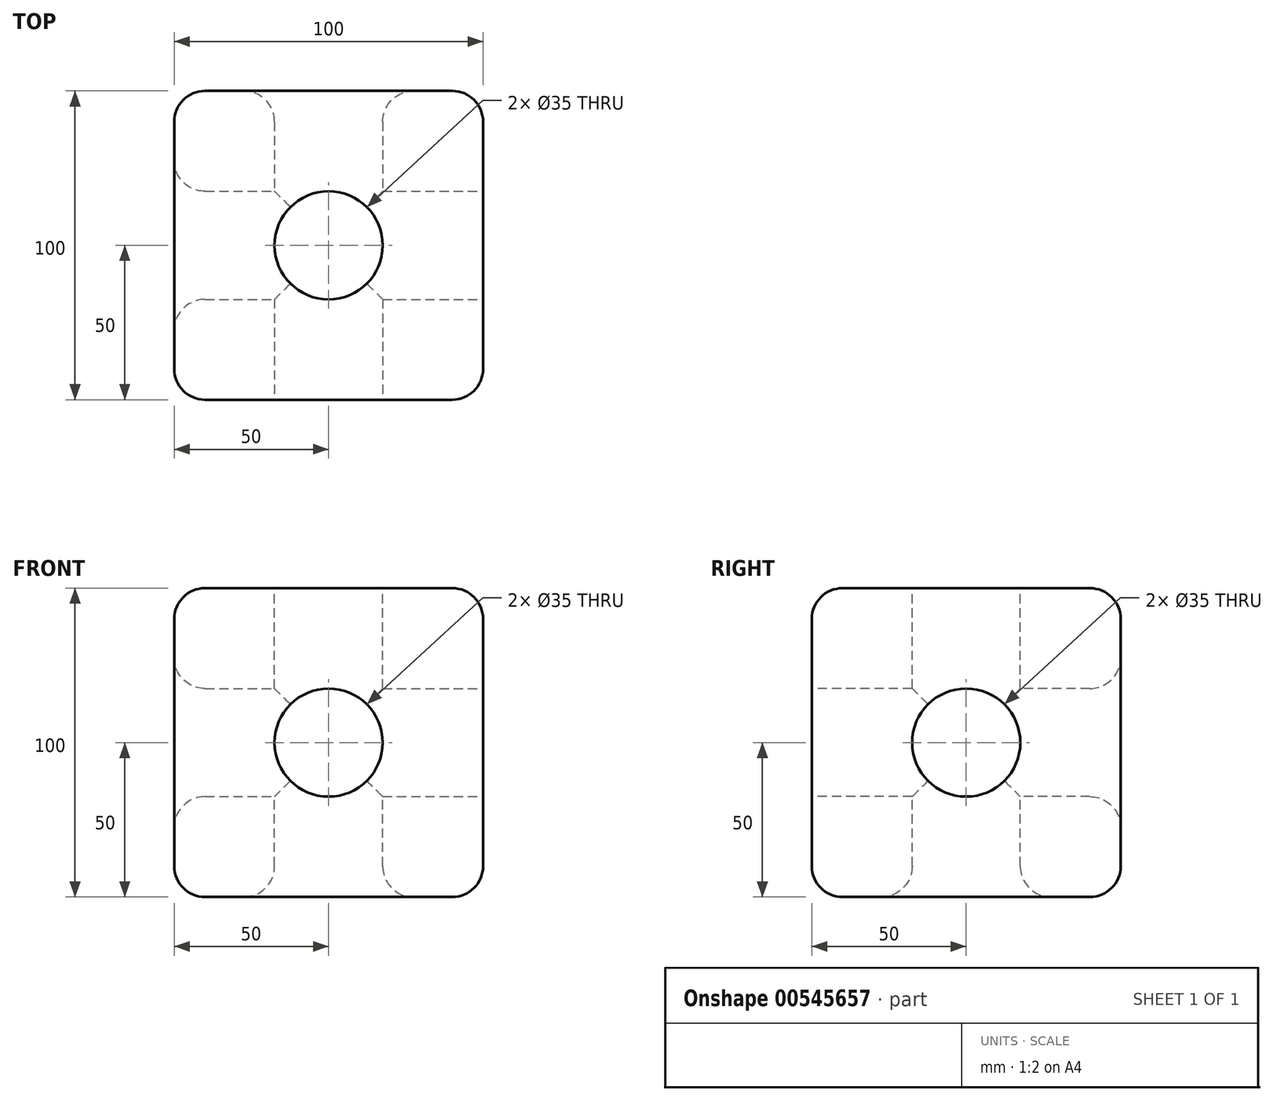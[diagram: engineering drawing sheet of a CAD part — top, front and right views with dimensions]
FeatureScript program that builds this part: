
annotation { "Feature Type Name" : "Feature", "Feature Type Description" : "" }
export const myFeature = defineFeature(function(context is Context, id is Id, definition is map)
    precondition{}
    {
        {
            var Q0;
            Q0=qCreatedBy(makeId("Front.planeOp"),FACE);
            var sketch = newSketch(context, id + "F0", { "sketchPlane" : qUnion([Q0])});
            skLineSegment(sketch, "E0.bottom", {"start": v(50, 50) * mm, "end": v(-50, 50) * mm});
            skLineSegment(sketch, "E0.top", {"start": v(50, -50) * mm, "end": v(-50, -50) * mm});
            skLineSegment(sketch, "E0.left", {"start": v(50, 50) * mm, "end": v(50, -50) * mm});
            skLineSegment(sketch, "E0.right", {"start": v(-50, 50) * mm, "end": v(-50, -50) * mm});
            skPoint(sketch, "E0.middle", {"position": v(0, 0) * mm});
            skSolve(sketch);
        }
        {
            var Q0;
            Q0=makeQuery(id+"F0.imprint","IMPRINT",FACE,{"disambiguationData":[TD([[makeQuery(id+"F0.imprint","IMPRINT",EDGE,{"derivedFrom":sQuery(id+"F0.wireOp",EDGE,"E0.bottom")}),1.0]])]});
            extrude(context, id + "F1", {"entities" : qUnion([Q0]), "endBound" : BoundingType.SYMMETRIC, "depth" : 100 * mm, "offsetDistance" : 25 * mm});
        }
        {
            var Q0;
            Q0=makeQuery(id+"F1.opExtrude","CAP_FACE",FACE,{"disambiguationData":[OSD([sQuery(id+"F0.wireOp",EDGE,"E0.bottom"),sQuery(id+"F0.wireOp",EDGE,"E0.top"),sQuery(id+"F0.wireOp",EDGE,"E0.left"),sQuery(id+"F0.wireOp",EDGE,"E0.right")])],"isStart":false});
            var sketch = newSketch(context, id + "F2", { "sketchPlane" : qUnion([Q0])});
            skCircle(sketch, "E1", {"center": v(0, 0) * mm, "radius": 17.5 * mm});
            skSolve(sketch);
        }
        {
            var Q0;
            Q0=makeQuery(id+"F2.imprint","IMPRINT",FACE,{"disambiguationData":[TD([[makeQuery(id+"F2.imprint","IMPRINT",EDGE,{"derivedFrom":sQuery(id+"F2.wireOp",EDGE,"E1")}),1.0]])]});
            extrude(context, id + "F3", {"entities" : qUnion([Q0]), "operationType" : NewBodyOperationType.REMOVE, "endBound" : BoundingType.THROUGH_ALL, "oppositeDirection" : true, "depth" : 25 * mm, "offsetDistance" : 25 * mm});
        }
        {
            var Q0;
            Q0=makeQuery(id+"F1.opExtrude","SWEPT_FACE",FACE,{"disambiguationData":[OSD([sQuery(id+"F0.wireOp",EDGE,"E0.left")])]});
            var sketch = newSketch(context, id + "F4", { "sketchPlane" : qUnion([Q0])});
            skCircle(sketch, "E2", {"center": v(0, 0) * mm, "radius": 17.5 * mm});
            skSolve(sketch);
        }
        {
            var Q0;
            Q0=makeQuery(id+"F4.imprint","IMPRINT",FACE,{"disambiguationData":[TD([[makeQuery(id+"F4.imprint","IMPRINT",EDGE,{"derivedFrom":sQuery(id+"F4.wireOp",EDGE,"E2")}),1.0]])]});
            extrude(context, id + "F5", {"entities" : qUnion([Q0]), "operationType" : NewBodyOperationType.REMOVE, "endBound" : BoundingType.THROUGH_ALL, "oppositeDirection" : true, "depth" : 25 * mm, "offsetDistance" : 25 * mm});
        }
        {
            var Q0;
            Q0=makeQuery(id+"F1.opExtrude","CAP_EDGE",EDGE,{"disambiguationData":[OSD([sQuery(id+"F0.wireOp",EDGE,"E0.bottom")])],"isStart":false});
            var Q1;
            Q1=makeQuery(id+"F1.opExtrude","CAP_EDGE",EDGE,{"disambiguationData":[OSD([sQuery(id+"F0.wireOp",EDGE,"E0.left")])],"isStart":false});
            var Q2;
            Q2=makeQuery(id+"F1.opExtrude","CAP_EDGE",EDGE,{"disambiguationData":[OSD([sQuery(id+"F0.wireOp",EDGE,"E0.top")])],"isStart":false});
            var Q3;
            Q3=makeQuery(id+"F1.opExtrude","CAP_EDGE",EDGE,{"disambiguationData":[OSD([sQuery(id+"F0.wireOp",EDGE,"E0.right")])],"isStart":false});
            var Q4;
            Q4=makeQuery(id+"F1.opExtrude","SWEPT_EDGE",EDGE,{"disambiguationData":[OSD([sQuery(id+"F0.wireOp",EDGE,"E0.top"),sQuery(id+"F0.wireOp",EDGE,"E0.left")])]});
            var Q5;
            Q5=makeQuery(id+"F1.opExtrude","SWEPT_EDGE",EDGE,{"disambiguationData":[OSD([sQuery(id+"F0.wireOp",EDGE,"E0.top"),sQuery(id+"F0.wireOp",EDGE,"E0.right")])]});
            var Q6;
            Q6=makeQuery(id+"F1.opExtrude","CAP_EDGE",EDGE,{"disambiguationData":[OSD([sQuery(id+"F0.wireOp",EDGE,"E0.top")])],"isStart":true});
            var Q7;
            Q7=makeQuery(id+"F1.opExtrude","CAP_EDGE",EDGE,{"disambiguationData":[OSD([sQuery(id+"F0.wireOp",EDGE,"E0.left")])],"isStart":true});
            var Q8;
            Q8=makeQuery(id+"F1.opExtrude","SWEPT_EDGE",EDGE,{"disambiguationData":[OSD([sQuery(id+"F0.wireOp",EDGE,"E0.bottom"),sQuery(id+"F0.wireOp",EDGE,"E0.left")])]});
            var Q9;
            Q9=makeQuery(id+"F1.opExtrude","CAP_EDGE",EDGE,{"disambiguationData":[OSD([sQuery(id+"F0.wireOp",EDGE,"E0.bottom")])],"isStart":true});
            var Q10;
            Q10=makeQuery(id+"F1.opExtrude","CAP_EDGE",EDGE,{"disambiguationData":[OSD([sQuery(id+"F0.wireOp",EDGE,"E0.right")])],"isStart":true});
            var Q11;
            Q11=makeQuery(id+"F1.opExtrude","SWEPT_EDGE",EDGE,{"disambiguationData":[OSD([sQuery(id+"F0.wireOp",EDGE,"E0.bottom"),sQuery(id+"F0.wireOp",EDGE,"E0.right")])]});
            var Q12;
            Q12=makeQuery(id+"F3.boolean.opBoolean","INTERSECT",EDGE,{"derivedFrom":[makeQuery(id+"F1.opExtrude","CAP_FACE",FACE,{"disambiguationData":[OSD([sQuery(id+"F0.wireOp",EDGE,"E0.bottom"),sQuery(id+"F0.wireOp",EDGE,"E0.top"),sQuery(id+"F0.wireOp",EDGE,"E0.left"),sQuery(id+"F0.wireOp",EDGE,"E0.right")])],"isStart":true}),makeQuery(id+"F3.opExtrude","SWEPT_FACE",FACE,{"disambiguationData":[OSD([sQuery(id+"F2.wireOp",EDGE,"E1")])]})]});
            var Q13;
            Q13=makeQuery(id+"F3.boolean.opBoolean","COPY",EDGE,{"derivedFrom":makeQuery(id+"F3.opExtrude","CAP_EDGE",EDGE,{"disambiguationData":[OSD([sQuery(id+"F2.wireOp",EDGE,"E1")])],"isStart":true})});
            fillet(context, id + "F6", {"entities" : qUnion([Q0, Q1, Q2, Q3, Q4, Q5, Q6, Q7, Q8, Q9, Q10, Q11, Q12, Q13]), "radius" : 10 * mm, "tangentPropagation" : true, "allowEdgeOverflow" : false});
        }
        {
            var Q0;
            Q0=makeQuery(id+"F5.boolean.opBoolean","COPY",EDGE,{"derivedFrom":makeQuery(id+"F5.opExtrude","CAP_EDGE",EDGE,{"disambiguationData":[OSD([sQuery(id+"F4.wireOp",EDGE,"E2")])],"isStart":true})});
            var Q1;
            Q1=makeQuery(id+"F5.boolean.opBoolean","INTERSECT",EDGE,{"derivedFrom":[makeQuery(id+"F1.opExtrude","SWEPT_FACE",FACE,{"disambiguationData":[OSD([sQuery(id+"F0.wireOp",EDGE,"E0.right")])]}),makeQuery(id+"F5.opExtrude","SWEPT_FACE",FACE,{"disambiguationData":[OSD([sQuery(id+"F4.wireOp",EDGE,"E2")])]})]});
            fillet(context, id + "F7", {"entities" : qUnion([Q0, Q1]), "radius" : 10 * mm, "tangentPropagation" : true, "allowEdgeOverflow" : false});
        }
        {
            var Q0;
            Q0=makeQuery(id+"F1.opExtrude","SWEPT_FACE",FACE,{"disambiguationData":[OSD([sQuery(id+"F0.wireOp",EDGE,"E0.bottom")])]});
            var sketch = newSketch(context, id + "F8", { "sketchPlane" : qUnion([Q0])});
            skCircle(sketch, "E3", {"center": v(0, 0) * mm, "radius": 17.5 * mm});
            skSolve(sketch);
        }
        {
            var Q0;
            Q0=makeQuery(id+"F8.imprint","IMPRINT",FACE,{"disambiguationData":[TD([[makeQuery(id+"F8.imprint","IMPRINT",EDGE,{"derivedFrom":sQuery(id+"F8.wireOp",EDGE,"E3")}),1.0]])]});
            extrude(context, id + "F9", {"entities" : qUnion([Q0]), "operationType" : NewBodyOperationType.REMOVE, "endBound" : BoundingType.THROUGH_ALL, "oppositeDirection" : true, "depth" : 25 * mm, "offsetDistance" : 25 * mm});
        }
        {
            var Q0;
            Q0=makeQuery(id+"F9.boolean.opBoolean","INTERSECT",EDGE,{"derivedFrom":[makeQuery(id+"F1.opExtrude","SWEPT_FACE",FACE,{"disambiguationData":[OSD([sQuery(id+"F0.wireOp",EDGE,"E0.top")])]}),makeQuery(id+"F9.opExtrude","SWEPT_FACE",FACE,{"disambiguationData":[OSD([sQuery(id+"F8.wireOp",EDGE,"E3")])]})]});
            var Q1;
            Q1=makeQuery(id+"F9.boolean.opBoolean","COPY",EDGE,{"derivedFrom":makeQuery(id+"F9.opExtrude","CAP_EDGE",EDGE,{"disambiguationData":[OSD([sQuery(id+"F8.wireOp",EDGE,"E3")])],"isStart":true})});
            fillet(context, id + "F10", {"entities" : qUnion([Q0, Q1]), "radius" : 10 * mm, "tangentPropagation" : true, "allowEdgeOverflow" : false});
        }
    });
